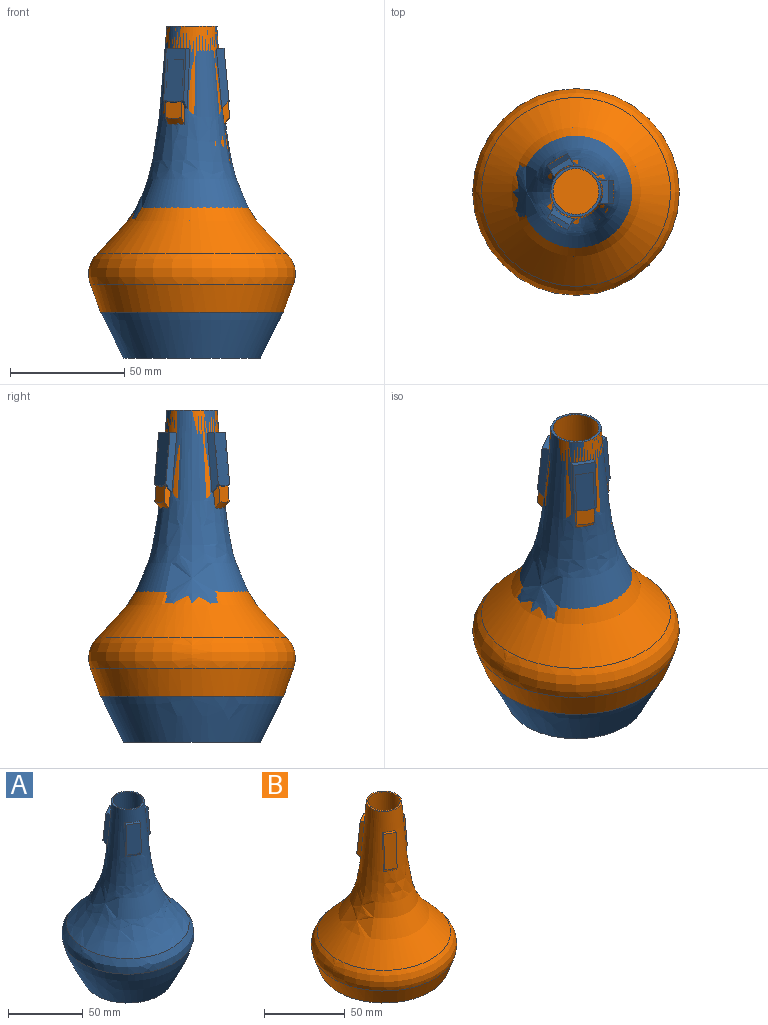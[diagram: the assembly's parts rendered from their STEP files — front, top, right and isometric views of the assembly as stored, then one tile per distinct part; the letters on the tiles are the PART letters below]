
ASSEMBLY  parts=2 mates=1
PART A: 30 faces, bbox 92.5x92.6x149 mm
  f0: plane 0.99x0.84mm, normal (-0.05,-0.08,-1), area 0.2mm2, adj f1,f2,f6
  f1: bspline ~10.82x7.68mm, area 40.1mm2, adj f0,f2,f4,f5,f6,f15
  f2: plane 30.21x8.79mm, normal (-0.87,0.5,0), area 84.8mm2, adj f0,f1,f3,f6,f15
  f3: plane 10.55x8.12mm, normal (0.05,0.08,1), area 26.2mm2, adj f2,f4,f6,f15
  f4: plane 30.21x8.79mm, normal (0.87,-0.5,0), area 84.8mm2, adj f1,f3,f5,f6,f15
  f5: plane 1.14x0.57mm, normal (-0.05,-0.08,-1), area 0.2mm2, adj f1,f4,f6
  f6: plane 23.34x9.76mm, normal (-0.5,-0.86,0.1), area 232.3mm2, adj f0,f1,f2,f3,f4,f5
  f7: plane 1.14x0.57mm, normal (-0.05,0.08,-1), area 0.2mm2, adj f8,f9,f13
  f8: bspline ~10.82x7.68mm, area 40.1mm2, adj f7,f9,f11,f12,f13,f15
  f9: plane 30.21x8.79mm, normal (0.87,0.5,0), area 84.8mm2, adj f7,f8,f10,f13,f15
  f10: plane 10.55x8.12mm, normal (0.05,-0.08,1), area 26.2mm2, adj f9,f11,f13,f15
  f11: plane 30.21x8.79mm, normal (-0.87,-0.5,0), area 84.8mm2, adj f8,f10,f12,f13,f15
  f12: plane 0.99x0.84mm, normal (-0.05,0.08,-1), area 0.2mm2, adj f8,f11,f13
  f13: plane 23.34x9.76mm, normal (-0.5,0.86,0.1), area 232.3mm2, adj f7,f8,f9,f10,f11,f12
  f14: plane 1.14x0.31mm, normal (0.1,0,-1), area 0.2mm2, adj f24,f28,f29
  f15: revolved ~100.83x82.08mm, area 25873.4mm2, adj f1,f2,f3,f4,f8,f9,f10,f11
  f16: plane 58.78x58.78mm, normal (0,0,1), area 2714mm2, adj f21
  f17: plane 60x60mm, normal (0,0,-1), area 2827.4mm2, adj f18
  f18: revolved ~88.04x88.04mm, area 8658.3mm2, adj f17,f23
  f19: plane 22x22mm, normal (0,0,1), area 66.1mm2, adj f15,f20
  f20: revolved ~101.15x79.94mm, area 12681.5mm2, adj f19,f22
  f21: revolved ~85.82x85.82mm, area 8092.8mm2, adj f16,f22
  f22: bspline ~86.43x86.39mm, area 3083mm2, adj f20,f21
  f23: bspline ~88.59x88.54mm, area 3130.8mm2, adj f15,f18
  f24: plane 30.21x9.53mm, normal (0,-1,0), area 84.8mm2, adj f14,f15,f25,f28,f29
  f25: plane 10.21x3.57mm, normal (-0.1,0,1), area 26.2mm2, adj f15,f24,f26,f28
  f26: plane 30.21x9.53mm, normal (0,1,0), area 84.8mm2, adj f15,f25,f27,f28,f29
  f27: plane 1.14x0.31mm, normal (0.1,0,-1), area 0.2mm2, adj f26,f28,f29
  f28: plane 23.34x10mm, normal (1,0,0.1), area 232.3mm2, adj f14,f24,f25,f26,f27,f29
  f29: bspline ~12.13x3.59mm, area 40.1mm2, adj f14,f15,f24,f26,f27,f28
PART B: 24 faces, bbox 96x96.1x130.7 mm
  f0: bspline ~8.76x6.42mm, area 31.6mm2, adj f1,f3,f4,f10
  f1: plane 33.91x10.13mm, normal (-0.87,0.5,0), area 76.8mm2, adj f0,f2,f4,f10
  f2: plane 8.44x6.53mm, normal (0.05,0.08,1), area 18.7mm2, adj f1,f3,f4,f10
  f3: plane 33.91x10.13mm, normal (0.87,-0.5,0), area 76.8mm2, adj f0,f2,f4,f10
  f4: plane 27.11x9.4mm, normal (-0.5,-0.86,0.09), area 204.4mm2, adj f0,f1,f2,f3
  f5: bspline ~8.76x6.42mm, area 31.6mm2, adj f6,f8,f9,f10
  f6: plane 33.91x10.13mm, normal (0.87,0.5,0), area 76.8mm2, adj f5,f7,f9,f10
  f7: plane 8.44x6.53mm, normal (0.05,-0.08,1), area 18.7mm2, adj f6,f8,f9,f10
  f8: plane 33.91x10.13mm, normal (-0.87,-0.5,0), area 76.8mm2, adj f5,f7,f9,f10
  f9: plane 27.11x9.4mm, normal (-0.5,0.86,0.09), area 204.4mm2, adj f5,f6,f7,f8
  f10: revolved ~99.34x82.48mm, area 25384.4mm2, adj f0,f1,f2,f3,f5,f6,f7,f8
  f11: plane 78.59x78.59mm, normal (0,0,1), area 4851mm2, adj f16
  f12: plane 80x80mm, normal (0,0,-1), area 5026.5mm2, adj f13
  f13: revolved ~88.64x88.64mm, area 3419.8mm2, adj f12,f18
  f14: plane 22x22mm, normal (0,0,1), area 66.1mm2, adj f10,f15
  f15: revolved ~99.62x80.2mm, area 12360.3mm2, adj f14,f17
  f16: revolved ~86.33x86.33mm, area 2995mm2, adj f11,f17
  f17: bspline ~88.03x87.98mm, area 3975.7mm2, adj f15,f16
  f18: bspline ~90.33x90.28mm, area 4085mm2, adj f10,f13
  f19: plane 33.91x10.81mm, normal (0,-1,0), area 76.8mm2, adj f10,f20,f22,f23
  f20: plane 8.12x2.91mm, normal (-0.09,0,1), area 18.7mm2, adj f10,f19,f21,f22
  f21: plane 33.91x10.81mm, normal (0,1,0), area 76.8mm2, adj f10,f20,f22,f23
  f22: plane 27.11x9.33mm, normal (1,0,0.09), area 204.4mm2, adj f19,f20,f21,f23
  f23: bspline ~9.5x3.06mm, area 31.6mm2, adj f10,f19,f21,f22
PLACE A t=(42.78,64.8,-27.8)mm
PLACE B t=(42.78,64.8,-7.8)mm
MATE fastened A.f19 <-> B.f14  axis (0,0,-1) through (42.78,64.8,117.2)mm
